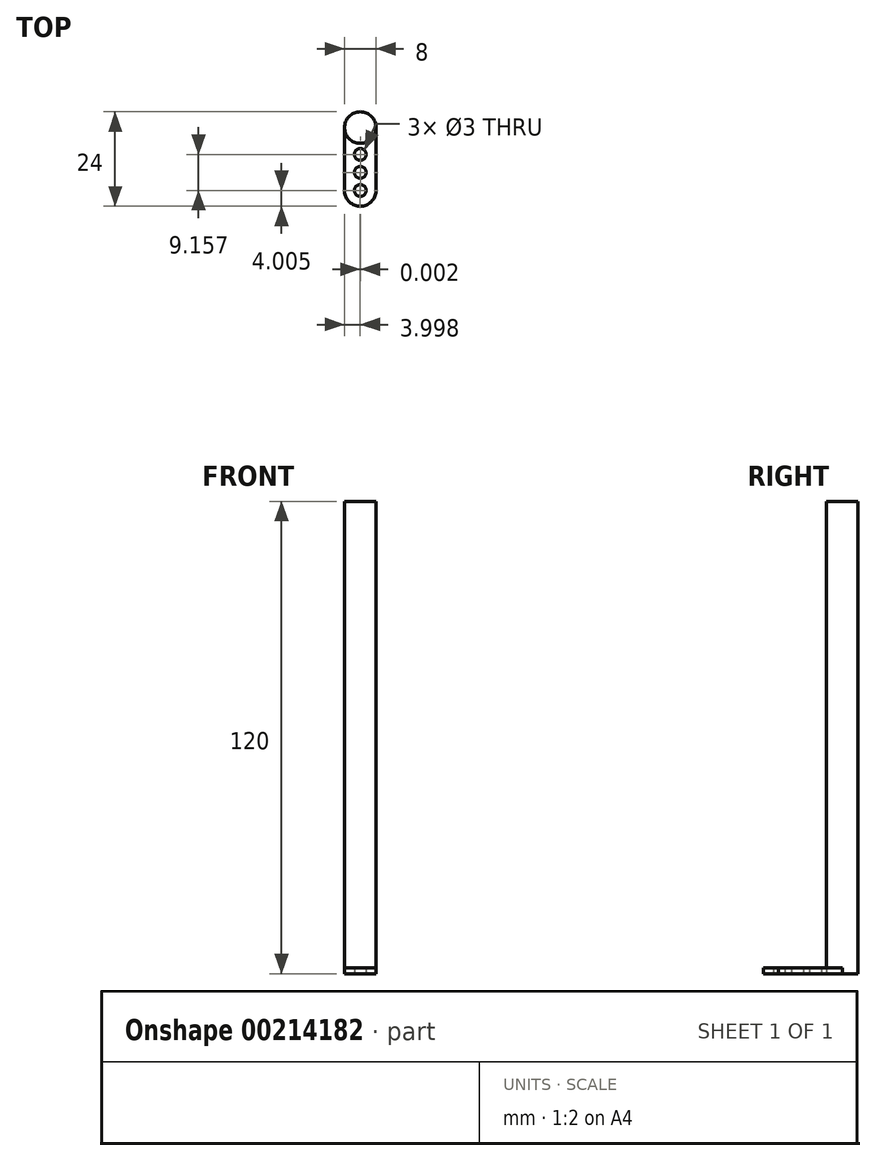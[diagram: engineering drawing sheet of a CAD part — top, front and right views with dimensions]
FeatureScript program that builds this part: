
annotation { "Feature Type Name" : "Feature", "Feature Type Description" : "" }
export const myFeature = defineFeature(function(context is Context, id is Id, definition is map)
    precondition{}
    {
        {
            var Q0;
            Q0=qCreatedBy(makeId("Top.planeOp"),FACE);
            var sketch = newSketch(context, id + "F0", { "sketchPlane" : qUnion([Q0])});
            skCircle(sketch, "E0", {"center": v(0, 0) * mm, "radius": 4 * mm});
            skSolve(sketch);
        }
        {
            var Q0;
            Q0=makeQuery(id+"F0.imprint","IMPRINT",FACE,{"disambiguationData":[TD([[makeQuery(id+"F0.imprint","IMPRINT",EDGE,{"derivedFrom":sQuery(id+"F0.wireOp",EDGE,"E0")}),1.0]])]});
            extrude(context, id + "F1", {"entities" : qUnion([Q0]), "depth" : 120 * mm});
        }
        {
            var Q0;
            Q0=makeQuery(id+"F1.opExtrude","CAP_FACE",FACE,{"disambiguationData":[OSD([sQuery(id+"F0.wireOp",EDGE,"E0")])],"isStart":true});
            var sketch = newSketch(context, id + "F2", { "sketchPlane" : qUnion([Q0])});
            skLineSegment(sketch, "E1.bottom", {"start": v(-4, 0) * mm, "end": v(4, 0) * mm});
            skLineSegment(sketch, "E1.left", {"start": v(-4, 0) * mm, "end": v(-4, 16.23) * mm});
            skLineSegment(sketch, "E1.right", {"start": v(4, 0) * mm, "end": v(4, 16.17) * mm});
            skArc(sketch, "E2", {"start": v(4, 16.17) * mm, "mid": v(0.03, 20) * mm, "end": v(-4, 16.23) * mm});
            skCircle(sketch, "E3", {"center": v(0, 6.84) * mm, "radius": 1.5 * mm});
            skCircle(sketch, "E4", {"center": v(0, 11.38) * mm, "radius": 1.5 * mm});
            skCircle(sketch, "E5", {"center": v(0, 16) * mm, "radius": 1.5 * mm});
            skSolve(sketch);
        }
        {
            var Q0;
            {var subQ1=sQuery(id+"F2.wireOp",EDGE,"E1.left");Q0=makeQuery(id+"F2.imprint","IMPRINT",FACE,{"disambiguationData":[TD([[makeQuery(id+"F2.imprint","IMPRINT",EDGE,{"derivedFrom":subQ1}),-1.0]])]});}
            extrude(context, id + "F3", {"entities" : qUnion([Q0]), "oppositeDirection" : true, "depth" : 1.5 * mm});
        }
    });
